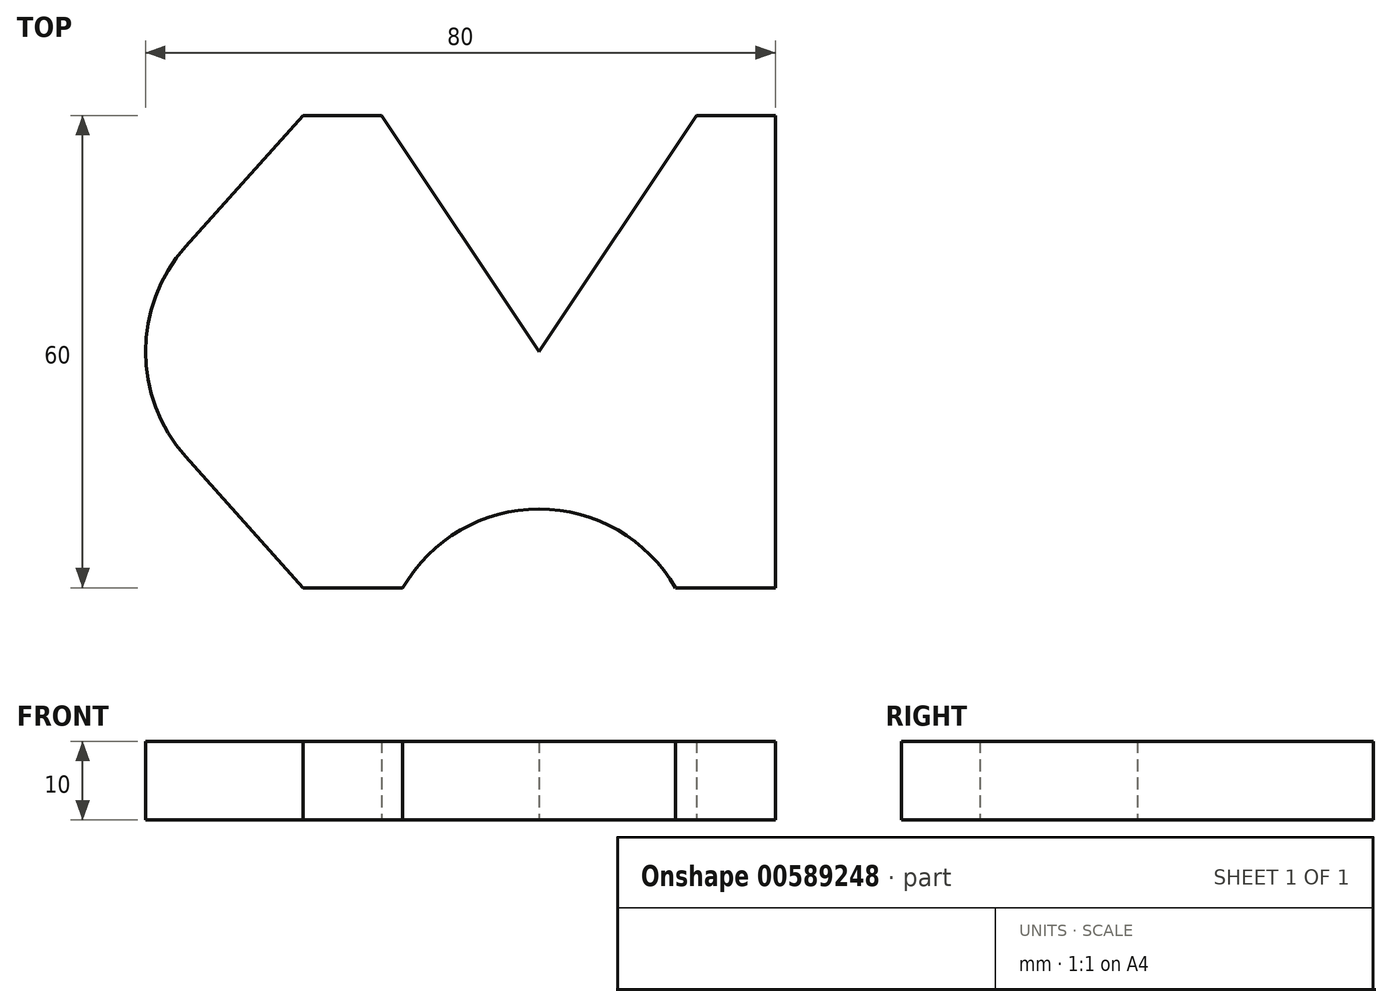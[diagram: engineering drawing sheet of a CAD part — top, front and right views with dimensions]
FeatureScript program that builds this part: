
annotation { "Feature Type Name" : "Feature", "Feature Type Description" : "" }
export const myFeature = defineFeature(function(context is Context, id is Id, definition is map)
    precondition{}
    {
        {
            var Q0;
            Q0=qCreatedBy(makeId("Top.planeOp"),FACE);
            var sketch = newSketch(context, id + "F0", { "sketchPlane" : qUnion([Q0])});
            skLineSegment(sketch, "E0", {"start": v(0, 0) * mm, "end": v(20, 30) * mm});
            skLineSegment(sketch, "E1", {"start": v(20, 30) * mm, "end": v(30, 30) * mm});
            skLineSegment(sketch, "E2", {"start": v(30, 30) * mm, "end": v(30, -30) * mm});
            skLineSegment(sketch, "E3", {"start": v(30, -30) * mm, "end": v(17.32, -30) * mm});
            skLineSegment(sketch, "E4", {"start": v(-17.32, -30) * mm, "end": v(-30, -30) * mm});
            skLineSegment(sketch, "E5", {"start": v(-30, -30) * mm, "end": v(-44.9, -13.33) * mm});
            skLineSegment(sketch, "E6", {"start": v(0, 0) * mm, "end": v(-20, 30) * mm});
            skLineSegment(sketch, "E7", {"start": v(-20, 30) * mm, "end": v(-30, 30) * mm});
            skLineSegment(sketch, "E8", {"start": v(-30, 30) * mm, "end": v(-44.9, 13.33) * mm});
            skArc(sketch, "E9", {"start": v(17.32, -30) * mm, "mid": v(0, -20) * mm, "end": v(-17.32, -30) * mm});
            skArc(sketch, "E10", {"start": v(-44.9, 13.33) * mm, "mid": v(-50, 0) * mm, "end": v(-44.9, -13.33) * mm});
            skLineSegment(sketch, "E11", {"start": v(-30, 30) * mm, "end": v(-30, -59.5) * mm, "construction": true});
            skSolve(sketch);
        }
        {
            var Q0;
            Q0 = qSketchRegion(id + "F0", true);
            extrude(context, id + "F1", {"entities" : qUnion([Q0]), "depth" : 10 * mm, "offsetDistance" : 25 * mm});
        }
    });
